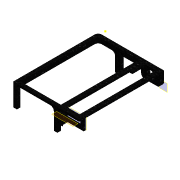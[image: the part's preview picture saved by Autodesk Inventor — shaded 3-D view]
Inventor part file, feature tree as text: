
AUTODESK INVENTOR PART (.ipt)
format: ipt  version: 2019.4 (Build 234330000, 330)  size: 427,008 bytes
history: native  units: mm
features: reference x23, other x14, sketch x12, extrude x10, projected_geometry x8, plane x3, hole x3, fillet x1, pattern_linear x1
ambient origin geometry x8: Origin, YZ Plane, XZ Plane, XY Plane, X Axis, Y Axis, Z Axis, Center Point
bodies: Solid1 (feature_tree)
feature tree (75):
  plane  "Work Plane1"
  extrude  "Extrusion1"  Depth=6.0mm
  extrude  "Extrusion2"  Depth=10.0mm TaperAngle=0.0deg
  plane  "Work Plane2"
  plane  "Work Plane5"
  extrude  "Extrusion6"  Depth=2.9mm
  extrude  "Extrusion12"  Depth=2.9mm
  hole  "Hole1"  [1 undecoded]
  extrude  "Extrusion13"  Depth=14.0mm
  fillet  "Fillet3"  Radius=53.0mm
  other  "Work Point1"
  hole  "Hole4"  [1 undecoded]
  sketch  "Sketch19"  dims[d41=3.8mm d42=6.0mm d43=7.0mm d44=4.0mm d45=90.0deg d46=50.0mm d47=20.594885mm d74=0.0mm]
  hole  "Hole5"  [1 undecoded]
  pattern_linear  "Rectangular Pattern2"  Count1=1  [1 undecoded]
  extrude  "Extrusion15"  Depth=10.0mm TaperAngle=0.0deg
  extrude  "Extrusion16"  Depth=10.0mm
  extrude  "Extrusion18"  Depth=12.0mm
  extrude  "Extrusion19"  Depth=12.0mm
  extrude  "Extrusion20"  Depth=12.0mm
  sketch  "Sketch1"  dims[d0=6.0mm d1=0.0mm d2=1.0mm]
  sketch  "Sketch2"  dims[d5=18.0mm d6=10.0mm d7=0.0mm]
  reference  "Reference4"
  reference  "Reference5"
  reference  "Reference6"
  reference  "Reference7"
  reference  "Reference8"
  reference  "Reference9"
  sketch  "Sketch6"  dims[d12=2.9mm d13=2.9mm]
  reference  "Reference33"
  reference  "Reference34"
  reference  "Reference35"
  reference  "Reference36"
  reference  "Reference37"
  reference  "Reference38"
  projected_geometry  "Projected Loop9"
  sketch  "Sketch14"  dims[d14=2.9mm d15=2.9mm]
  projected_geometry  "Projected Loop10"
  projected_geometry  "Projected Loop11"
  projected_geometry  "Projected Loop12"
  projected_geometry  "Projected Loop13"
  reference  "Reference41"
  sketch  "Sketch18"  dims[d37=10.0mm d38=0.0mm]
  projected_geometry  "Projected Loop15"
  sketch  "Sketch20"  dims[d76=14.0mm d77=14.0mm d79=53.0mm]
  reference  "Reference43"
  reference  "Reference44"
  reference  "Reference45"
  reference  "Reference46"
  reference  "Reference47"
  sketch  "Sketch21"  dims[d81=0.0mm d83=64.0mm]
  reference  "Reference48"
  reference  "Reference49"
  sketch  "Sketch22"  dims[d84=6.0mm d85=10.0mm]
  projected_geometry  "Projected Loop16"
  sketch  "Sketch24"  dims[d86=10.0mm]
  reference  "Reference52"
  sketch  "Sketch25"  dims[d87=10.0mm d88=0.0mm d90=10.0mm]
  projected_geometry  "Projected Loop18"
  reference  "Reference53"
  sketch  "Sketch26"  dims[d91=10.0mm d92=10.0mm d93=0.0mm d94=10.0mm d95=12.0mm d96=12.0mm d97=12.0mm d110=5.0mm d111=2.8mm d112=6.0mm d113=7.0mm d114=4.0mm d115=90.0deg d116=20.0mm d117=20.594885mm d118=105.0mm d119=2.8mm d120=6.0mm d121=4.0mm d122=2.0mm d123=90.0deg d124=8.0mm d125=0.0mm d126=150.0mm d128=12.5mm d129=10.0mm d130=30.0mm d132=10.0mm d133=5.0mm d134=0.0mm d135=10.0mm d138=3.0mm d139=0.0mm d140=9.0mm d141=10.0mm d146=2.8mm d147=20.0mm d148=0.0mm d149=14.0mm d150=2.0mm d151=5.0mm d152=0.0mm d153=2.5mm d154=2.5mm d155=2.5mm d156=2.5mm d157=10.0mm d158=0.0mm]
  reference  "Reference54"
  other  "Assembly_opentrons_microscope_slide_y_base.iam"
  other  "00_NEMA11:1"
  other  "Lagerschild_11_1"
  other  "Assembly_spindeldrive_350mm_2:1"
  other  "00_spindel_350mm:1"
  other  "00_spindel_bearings:1"
  other  "Assembly_Opentrons_Imagingunit_v2.iam"
  other  "00_MGN12 LINEAR GUIDE RAIL, CONFIGURABLE:2"
  other  "00_spindel_bearings:2"
  other  "00_MGN12 LINEAR GUIDE RAIL, CONFIGURABLE:1"
  other  "09_Opentrons_Microscope_Baseplate:1"
  other  "00_Endstop:1"
  other  "Assembly_Opentrons_Imagingunit_v0.iam"
note: 4 required parameter values undecoded (feature->parameter linkage not recoverable at this tier; creation-order binding heuristic only, values carry confidence <= 0.55)
